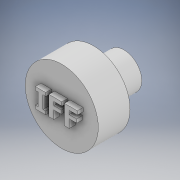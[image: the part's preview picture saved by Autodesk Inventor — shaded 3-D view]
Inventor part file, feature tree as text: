
AUTODESK INVENTOR PART (.ipt)
format: ipt  version: 2022 (Build 260153000, 153)  size: 153,600 bytes
history: native  units: in
note: dims shown in document units (in); Inventor stores cm internally (conversion verified against a paired STEP export)
features: sketch x3, extrude x3
ambient origin geometry x8: Origin, YZ Plane, XZ Plane, XY Plane, X Axis, Y Axis, Z Axis, Center Point
bodies: Solid1 (feature_tree)
feature tree (6):
  sketch  "Sketch1"  dims[d0=0.4898in d1=0.0185in]
  extrude  "Extrusion1"  Depth=0.0185in
  extrude  "Extrusion2"  Depth=0.189in TaperAngle=0.0deg
  sketch  "Sketch2"  dims[d2=0.1969in d3=0.0in d4=0.189in d5=0.0in]
  extrude  "Extrusion4"  [1 undecoded]
  sketch  "Sketch3"  dims[d8=0.0354in d9=0.0in]
note: 1 required parameter value undecoded (feature->parameter linkage not recoverable at this tier; creation-order binding heuristic only, values carry confidence <= 0.55)
